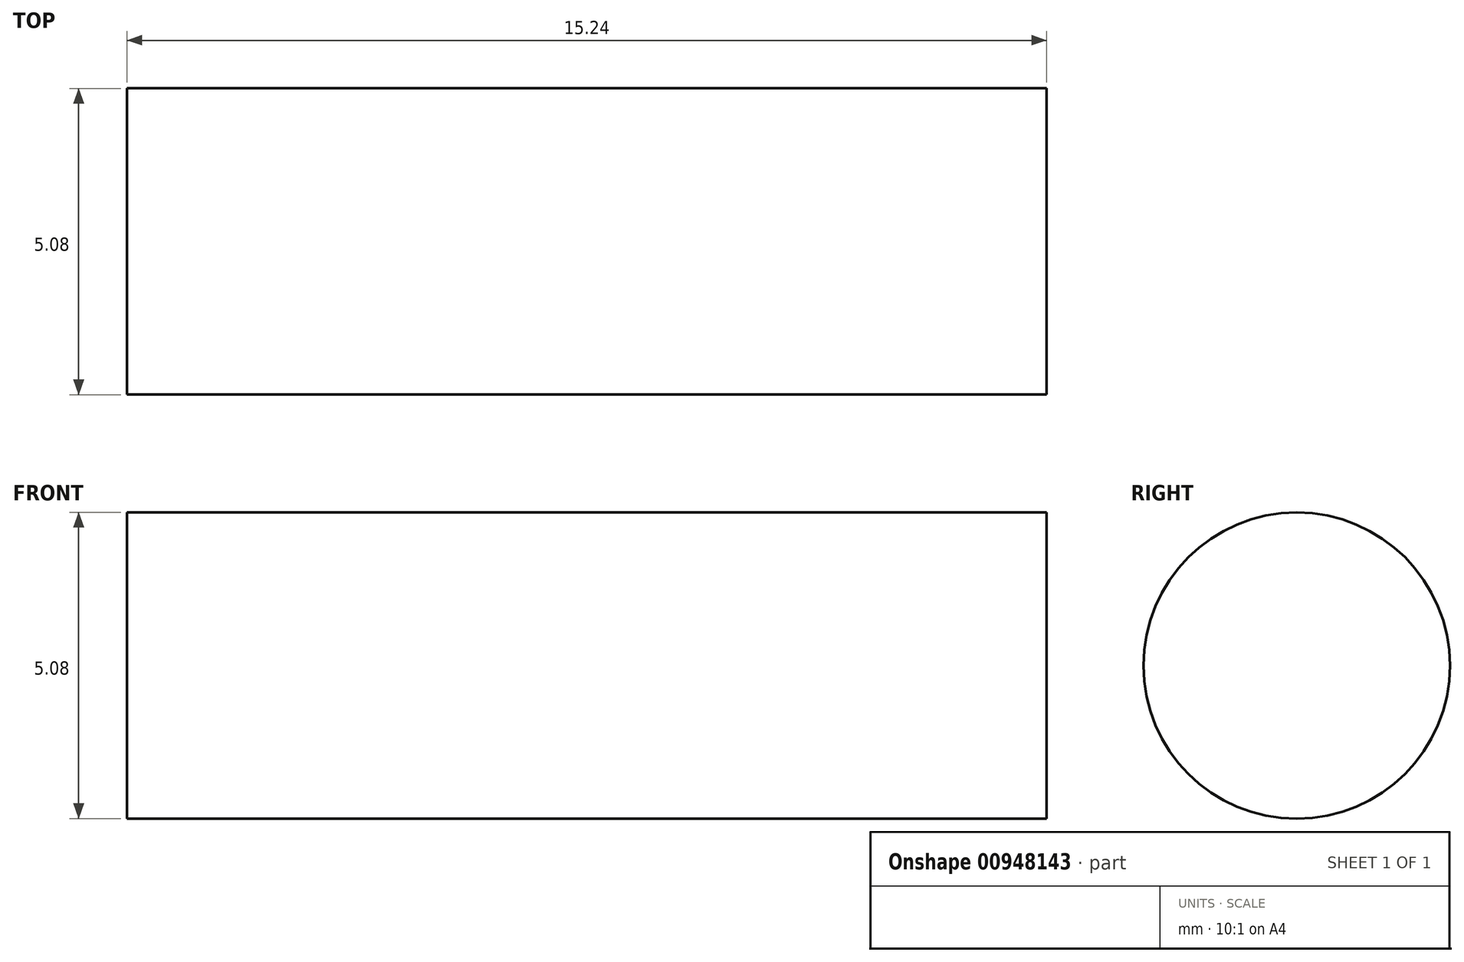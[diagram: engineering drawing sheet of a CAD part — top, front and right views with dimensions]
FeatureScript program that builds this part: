
annotation { "Feature Type Name" : "Feature", "Feature Type Description" : "" }
export const myFeature = defineFeature(function(context is Context, id is Id, definition is map)
    precondition{}
    {
        {
            var Q0;
            Q0=qCreatedBy(makeId("Right.planeOp"),FACE);
            var sketch = newSketch(context, id + "F0", { "sketchPlane" : qUnion([Q0])});
            skCircle(sketch, "E0", {"center": v(-23.34, 11.4) * mm, "radius": 2.54 * mm});
            skSolve(sketch);
        }
        {
            var Q0;
            Q0=makeQuery(id+"F0.imprint","IMPRINT",FACE,{"disambiguationData":[TD([[makeQuery(id+"F0.imprint","IMPRINT",EDGE,{"derivedFrom":sQuery(id+"F0.wireOp",EDGE,"E0")}),1.0]])]});
            extrude(context, id + "F1", {"entities" : qUnion([Q0]), "depth" : 15.24 * mm, "offsetDistance" : 25.4 * mm});
        }
    });
